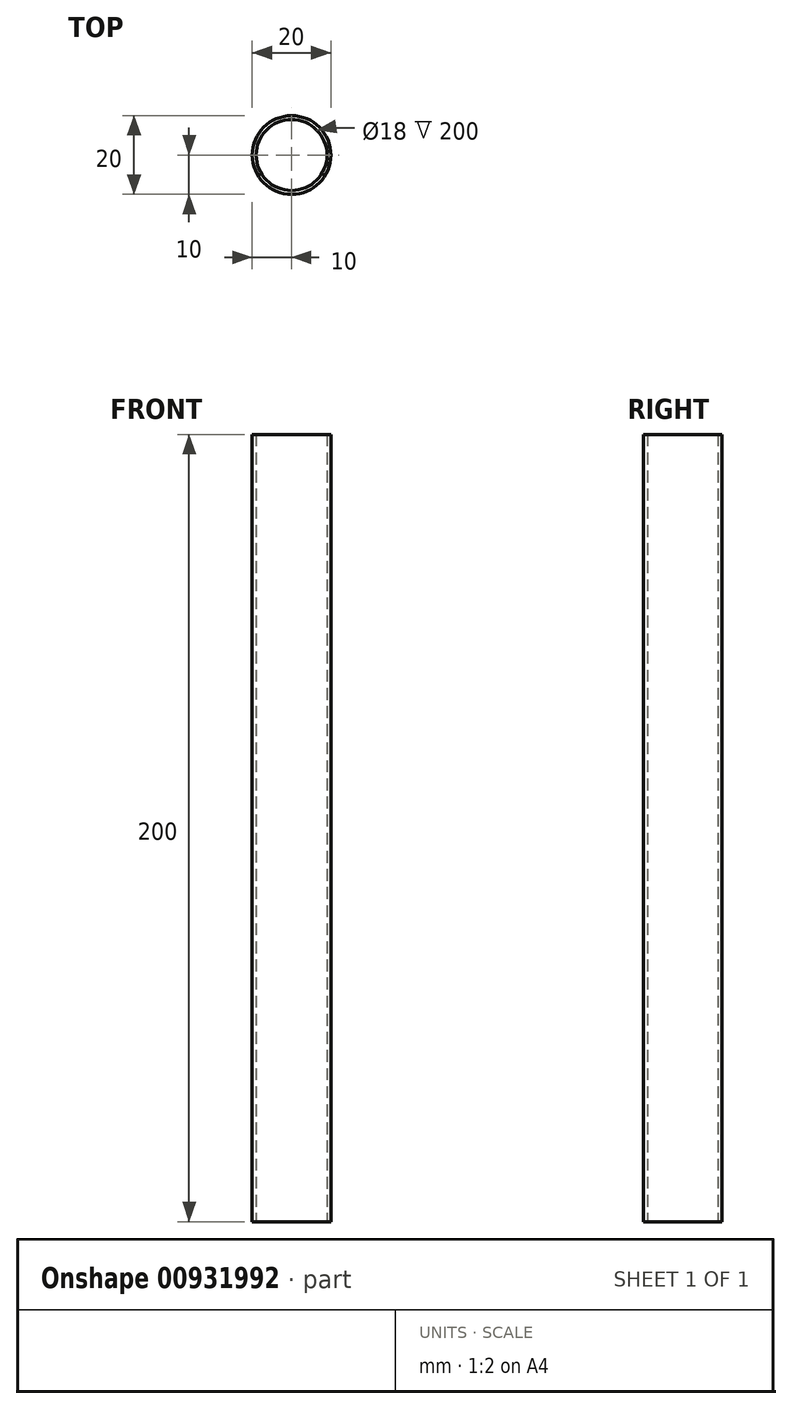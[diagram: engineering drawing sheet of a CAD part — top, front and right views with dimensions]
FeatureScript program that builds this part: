
annotation { "Feature Type Name" : "Feature", "Feature Type Description" : "" }
export const myFeature = defineFeature(function(context is Context, id is Id, definition is map)
    precondition{}
    {
        {
            var Q0;
            Q0=qCreatedBy(makeId("Top.planeOp"),FACE);
            var sketch = newSketch(context, id + "F0", { "sketchPlane" : qUnion([Q0])});
            skCircle(sketch, "E0", {"center": v(0, 0) * mm, "radius": 10 * mm});
            skCircle(sketch, "E1", {"center": v(0, 0) * mm, "radius": 9 * mm});
            skSolve(sketch);
        }
        {
            var Q0;
            Q0 = qSketchRegion(id + "F0", true);
            extrude(context, id + "F1", {"entities" : qUnion([Q0]), "depth" : 200 * mm, "offsetDistance" : 25 * mm});
        }
    });
